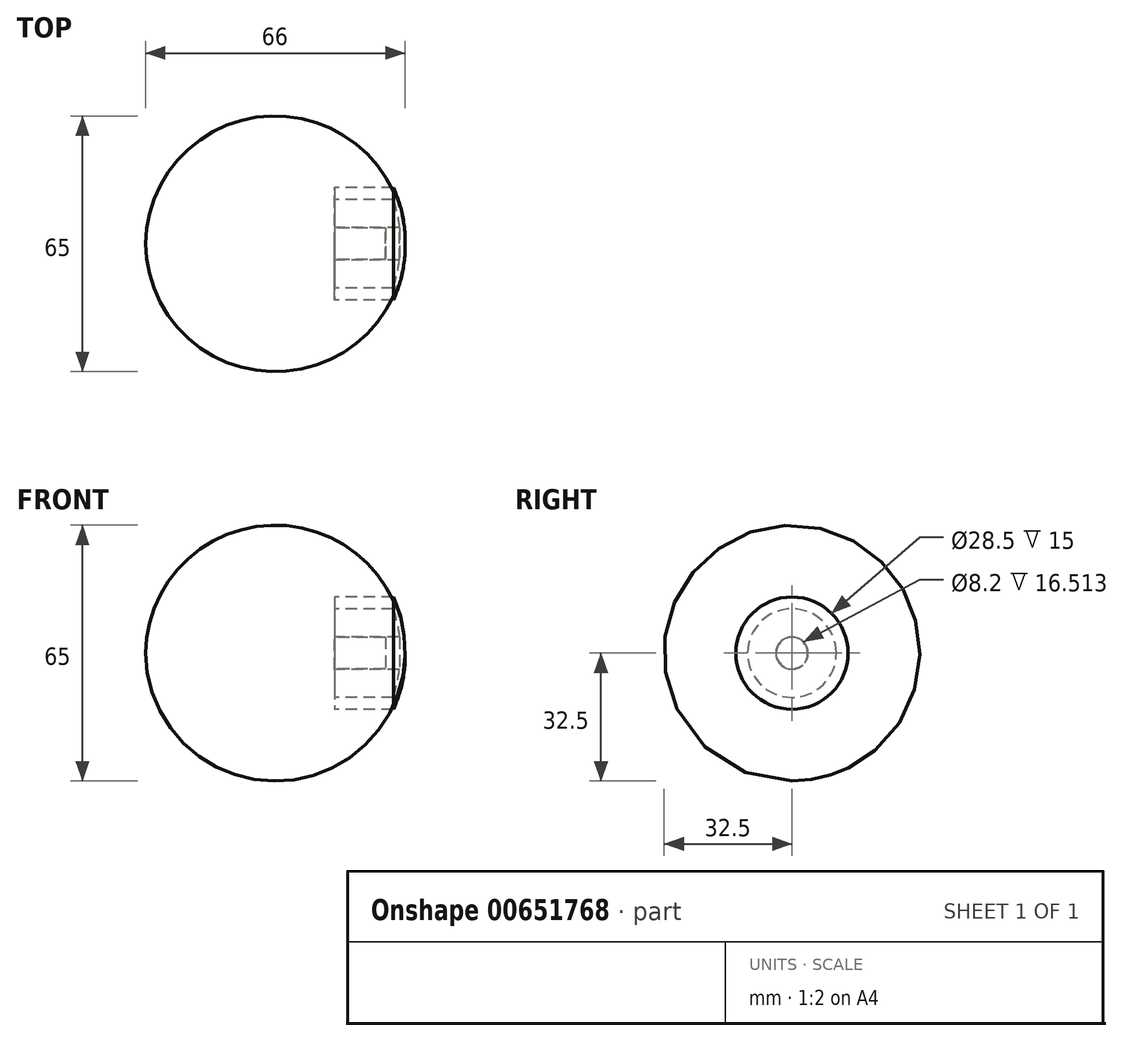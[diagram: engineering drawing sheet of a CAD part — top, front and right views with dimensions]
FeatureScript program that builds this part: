
annotation { "Feature Type Name" : "Feature", "Feature Type Description" : "" }
export const myFeature = defineFeature(function(context is Context, id is Id, definition is map)
    precondition{}
    {
        {
            var Q0;
            Q0=qCreatedBy(makeId("Top.planeOp"),FACE);
            var sketch = newSketch(context, id + "F0", { "sketchPlane" : qUnion([Q0])});
            skLineSegment(sketch, "E0.bottom", {"start": v(0, 11.25) * mm, "end": v(15, 11.25) * mm});
            skLineSegment(sketch, "E0.top", {"start": v(0, 14.25) * mm, "end": v(15, 14.25) * mm});
            skLineSegment(sketch, "E0.left", {"start": v(0, 11.25) * mm, "end": v(0, 14.25) * mm});
            skLineSegment(sketch, "E0.right", {"start": v(15, 11.25) * mm, "end": v(15, 14.25) * mm});
            skLineSegment(sketch, "E1", {"start": v(0, 0) * mm, "end": v(18, 0) * mm, "construction": true});
            skLineSegment(sketch, "E2", {"start": v(0, 0) * mm, "end": v(0, 4.63) * mm, "construction": true});
            skArc(sketch, "E3", {"start": v(18, 0) * mm, "mid": v(17.3, 7.3) * mm, "end": v(15, 14.25) * mm});
            skArc(sketch, "E4", {"start": v(16.84, 0) * mm, "mid": v(16.28, 5.68) * mm, "end": v(15, 11.25) * mm});
            skLineSegment(sketch, "E5", {"start": v(18, 0) * mm, "end": v(16.84, 0) * mm});
            skSolve(sketch);
        }
        {
            var Q0;
            Q0=makeQuery(id+"F0.imprint","IMPRINT",FACE,{"disambiguationData":[TD([[makeQuery(id+"F0.imprint","IMPRINT",EDGE,{"derivedFrom":sQuery(id+"F0.wireOp",EDGE,"E0.right")}),-1.0]])]});
            var Q1;
            Q1=makeQuery(id+"F0.imprint","IMPRINT",FACE,{"disambiguationData":[TD([[makeQuery(id+"F0.imprint","IMPRINT",EDGE,{"derivedFrom":sQuery(id+"F0.wireOp",EDGE,"E0.bottom")}),1.0]])]});
            var Q2;
            Q2=sQuery(id+"F0.wireOp",EDGE,"E0.left");
            var Q3;
            Q3=sQuery(id+"F0.wireOp",EDGE,"E0.top");
            var Q4;
            Q4=sQuery(id+"F0.wireOp",EDGE,"E0.bottom");
            var Q5;
            Q5=sQuery(id+"F0.wireOp",EDGE,"E3");
            var Q6;
            Q6=sQuery(id+"F0.wireOp",EDGE,"E4");
            var Q7;
            Q7=sQuery(id+"F0.wireOp",EDGE,"E1");
            revolve(context, id + "F1", {"entities" : qUnion([Q0, Q1]), "surfaceEntities" : qUnion([Q2, Q3, Q4, Q5, Q6]), "axis" : qUnion([Q7]), "revolveType" : RevolveType.FULL, "surfaceOperationType" : NewSurfaceOperationType.NEW});
        }
        {
            var Q0;
            Q0=qCreatedBy(makeId("Right.planeOp"),FACE);
            var sketch = newSketch(context, id + "F2", { "sketchPlane" : qUnion([Q0])});
            skCircle(sketch, "E6", {"center": v(0, 0) * mm, "radius": 4.1 * mm});
            skSolve(sketch);
        }
        {
            var Q0;
            Q0=makeQuery(id+"F2.imprint","IMPRINT",FACE,{"disambiguationData":[TD([[makeQuery(id+"F2.imprint","IMPRINT",EDGE,{"derivedFrom":sQuery(id+"F2.wireOp",EDGE,"E6")}),1.0]])]});
            extrude(context, id + "F3", {"entities" : qUnion([Q0]), "operationType" : NewBodyOperationType.ADD, "endBound" : BoundingType.UP_TO_NEXT, "depth" : 16 * mm, "offsetDistance" : 25 * mm});
        }
        {
            var Q0;
            Q0=makeQuery(id+"F3.opExtrude","CAP_FACE",FACE,{"disambiguationData":[OSD([sQuery(id+"F2.wireOp",EDGE,"E6")])],"isStart":true});
            var sketch = newSketch(context, id + "F4", { "sketchPlane" : qUnion([Q0])});
            skCircle(sketch, "E7", {"center": v(0, 0) * mm, "radius": 4 * mm});
            skSolve(sketch);
        }
        {
            var Q0;
            Q0=makeQuery(id+"F4.imprint","IMPRINT",FACE,{"disambiguationData":[TD([[makeQuery(id+"F4.imprint","IMPRINT",EDGE,{"derivedFrom":sQuery(id+"F4.wireOp",EDGE,"E7")}),1.0]])]});
            extrude(context, id + "F5", {"entities" : qUnion([Q0]), "operationType" : NewBodyOperationType.REMOVE, "oppositeDirection" : true, "depth" : 13 * mm, "offsetDistance" : 25 * mm});
        }
    });
